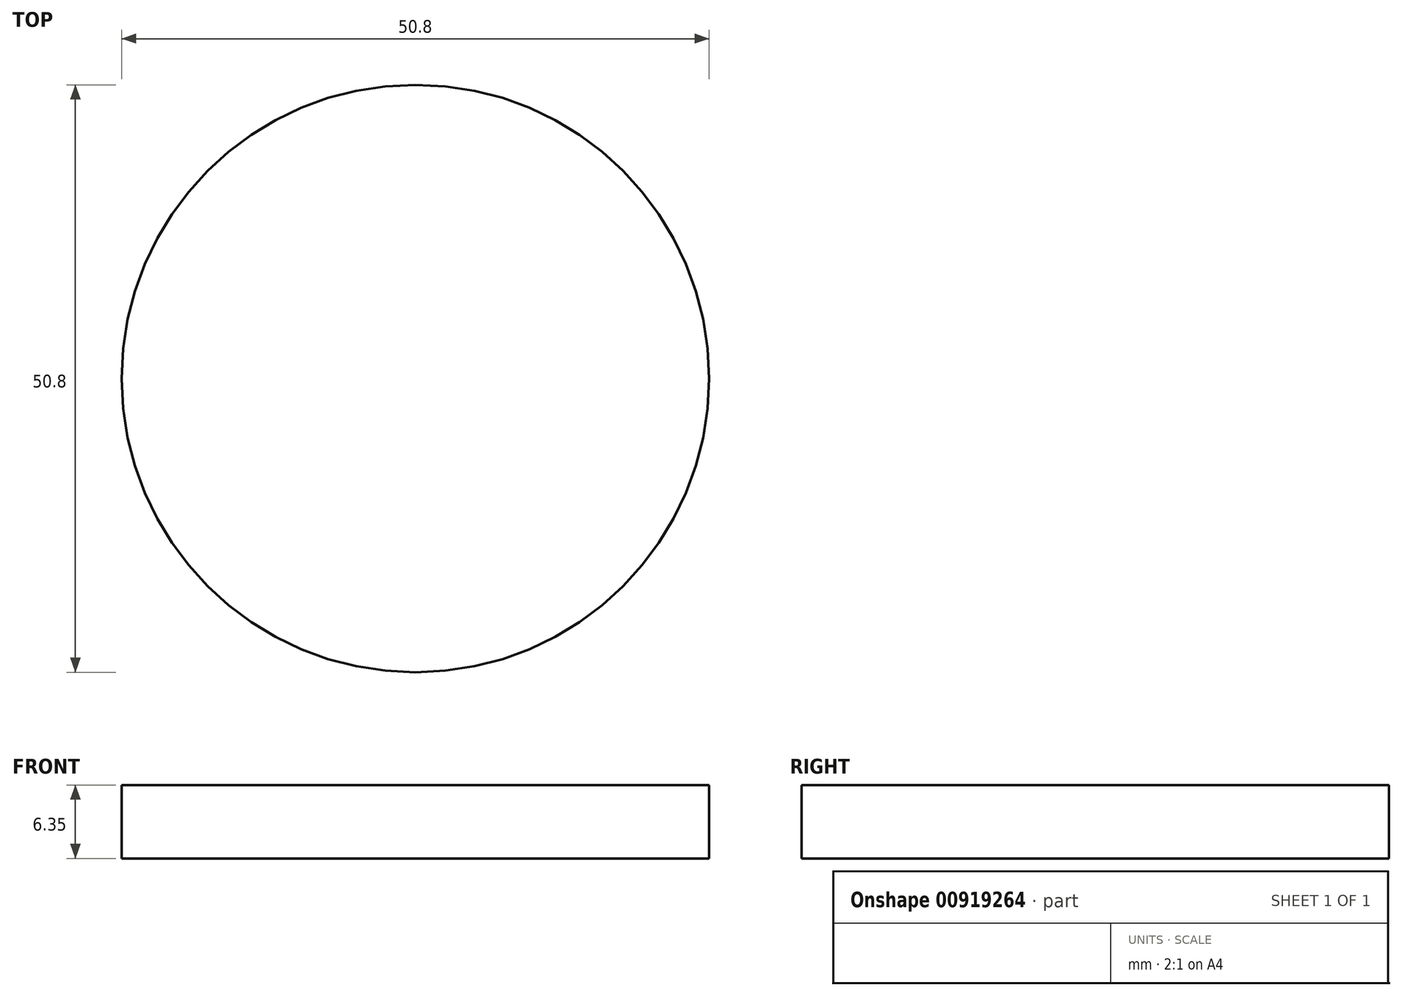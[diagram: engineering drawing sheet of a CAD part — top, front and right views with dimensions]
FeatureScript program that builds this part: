
annotation { "Feature Type Name" : "Feature", "Feature Type Description" : "" }
export const myFeature = defineFeature(function(context is Context, id is Id, definition is map)
    precondition{}
    {
        {
            var Q0;
            Q0=qCreatedBy(makeId("Top.planeOp"),FACE);
            var sketch = newSketch(context, id + "F0", { "sketchPlane" : qUnion([Q0])});
            skCircle(sketch, "E0", {"center": v(0, 0) * mm, "radius": 25.4 * mm});
            skSolve(sketch);
        }
        {
            var Q0;
            Q0=makeQuery(id+"F0.imprint","IMPRINT",FACE,{"disambiguationData":[TD([[makeQuery(id+"F0.imprint","IMPRINT",EDGE,{"derivedFrom":sQuery(id+"F0.wireOp",EDGE,"E0")}),1.0]])]});
            extrude(context, id + "F1", {"entities" : qUnion([Q0]), "depth" : 6.35 * mm, "offsetDistance" : 25.4 * mm});
        }
    });
